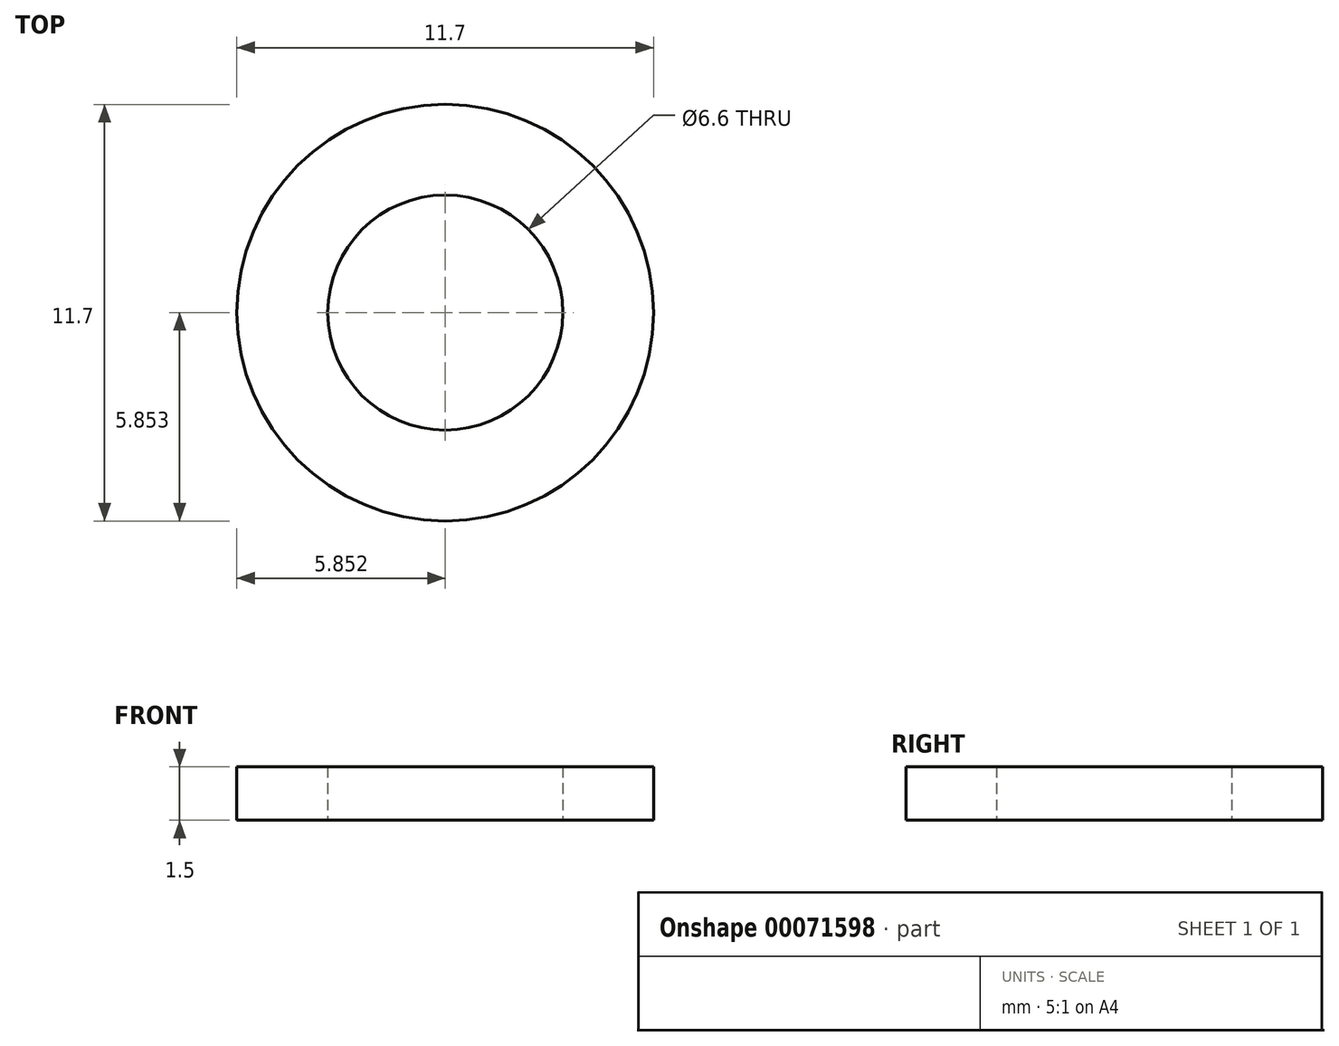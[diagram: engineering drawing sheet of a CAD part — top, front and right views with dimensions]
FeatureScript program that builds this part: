
annotation { "Feature Type Name" : "Feature", "Feature Type Description" : "" }
export const myFeature = defineFeature(function(context is Context, id is Id, definition is map)
    precondition{}
    {
        {
            var Q0;
            Q0=qCreatedBy(makeId("Top.planeOp"),FACE);
            var sketch = newSketch(context, id + "F0", { "sketchPlane" : qUnion([Q0])});
            skCircle(sketch, "E0", {"center": v(14.67, 14.61) * mm, "radius": 5.85 * mm});
            skCircle(sketch, "E1", {"center": v(14.67, 14.61) * mm, "radius": 3.3 * mm});
            skSolve(sketch);
        }
        {
            var Q0;
            Q0=qSketchRegion(id+"F0",true);
            extrude(context, id + "F1", {"entities" : qUnion([Q0]), "depth" : 1.5 * mm});
        }
    });
